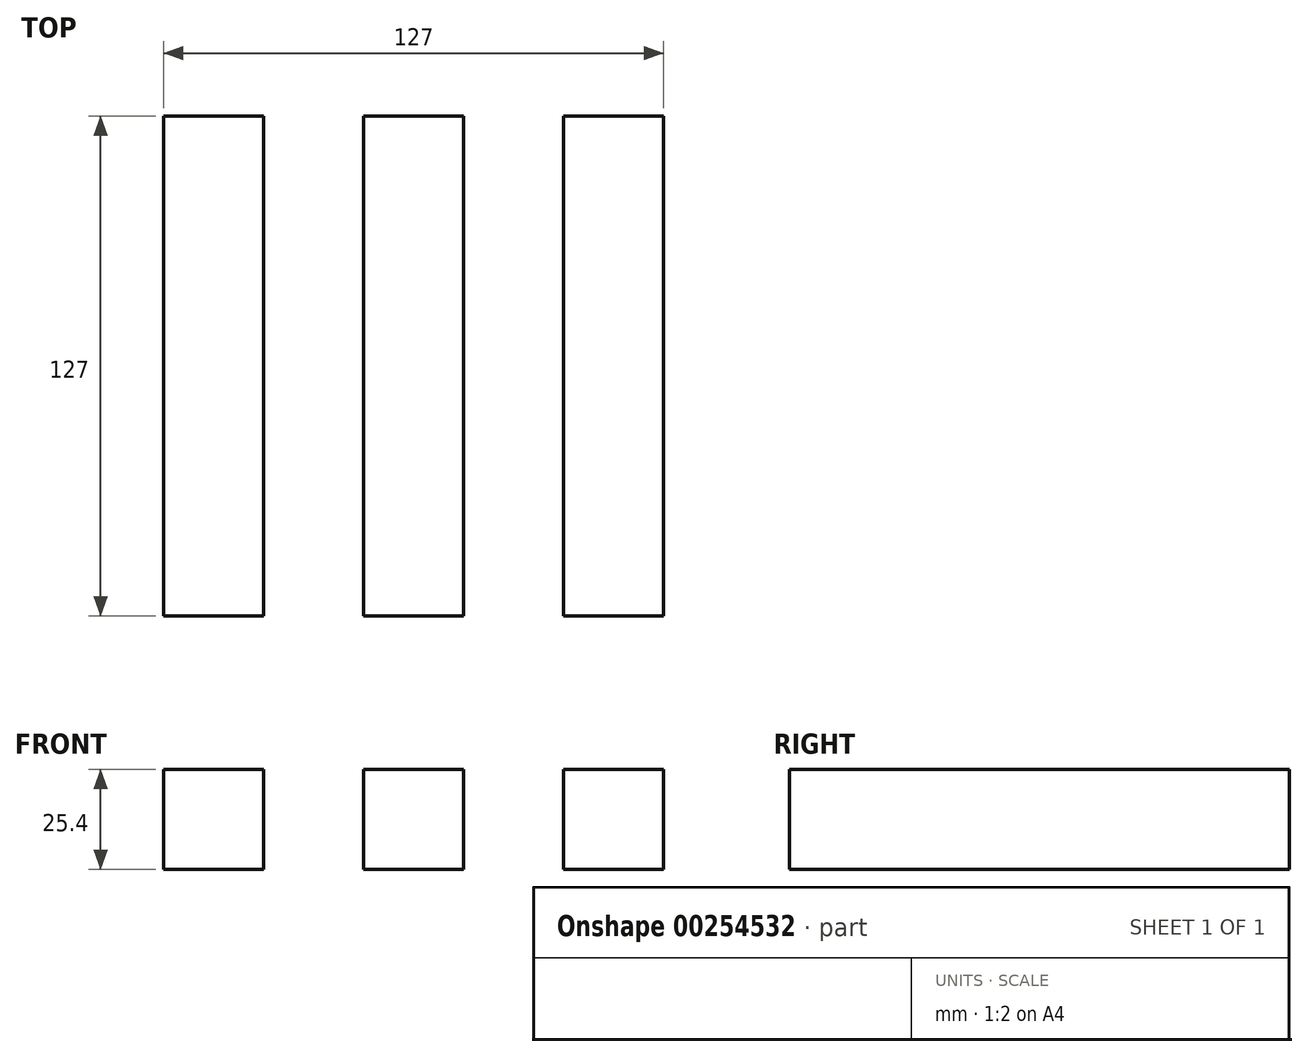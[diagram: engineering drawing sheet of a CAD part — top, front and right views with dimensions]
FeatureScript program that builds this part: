
annotation { "Feature Type Name" : "Feature", "Feature Type Description" : "" }
export const myFeature = defineFeature(function(context is Context, id is Id, definition is map)
    precondition{}
    {
        {
            var Q0;
            Q0=qCreatedBy(makeId("Front.planeOp"),FACE);
            var sketch = newSketch(context, id + "F0", { "sketchPlane" : qUnion([Q0])});
            skLineSegment(sketch, "E0.bottom", {"start": v(-12.7, 12.7) * mm, "end": v(12.7, 12.7) * mm});
            skLineSegment(sketch, "E0.top", {"start": v(-12.7, -12.7) * mm, "end": v(12.7, -12.7) * mm});
            skLineSegment(sketch, "E0.left", {"start": v(-12.7, 12.7) * mm, "end": v(-12.7, -12.7) * mm});
            skLineSegment(sketch, "E0.right", {"start": v(12.7, 12.7) * mm, "end": v(12.7, -12.7) * mm});
            skPoint(sketch, "E0.middle", {"position": v(0, 0) * mm});
            skLineSegment(sketch, "E1", {"start": v(0, 0) * mm, "end": v(-50.8, 0) * mm});
            skLineSegment(sketch, "E2", {"start": v(0, 0) * mm, "end": v(50.8, 0) * mm});
            skLineSegment(sketch, "E3.bottom", {"start": v(-38.1, -12.7) * mm, "end": v(-63.5, -12.7) * mm});
            skLineSegment(sketch, "E3.top", {"start": v(-38.1, 12.7) * mm, "end": v(-63.5, 12.7) * mm});
            skLineSegment(sketch, "E3.left", {"start": v(-38.1, -12.7) * mm, "end": v(-38.1, 12.7) * mm});
            skLineSegment(sketch, "E3.right", {"start": v(-63.5, -12.7) * mm, "end": v(-63.5, 12.7) * mm});
            skPoint(sketch, "E3.middle", {"position": v(-50.8, 0) * mm});
            skLineSegment(sketch, "E4.bottom", {"start": v(63.5, -12.7) * mm, "end": v(38.1, -12.7) * mm});
            skLineSegment(sketch, "E4.top", {"start": v(63.5, 12.7) * mm, "end": v(38.1, 12.7) * mm});
            skLineSegment(sketch, "E4.left", {"start": v(63.5, -12.7) * mm, "end": v(63.5, 12.7) * mm});
            skLineSegment(sketch, "E4.right", {"start": v(38.1, -12.7) * mm, "end": v(38.1, 12.7) * mm});
            skPoint(sketch, "E4.middle", {"position": v(50.8, 0) * mm});
            skSolve(sketch);
        }
        {
            var Q0;
            {var subQ1=sQuery(id+"F0.wireOp",EDGE,"E4.bottom");Q0=makeQuery(id+"F0.imprint","IMPRINT",FACE,{"disambiguationData":[TD([[makeQuery(id+"F0.imprint","IMPRINT",EDGE,{"derivedFrom":subQ1}),-1.0]])]});}
            var Q1;
            {var subQ6=sQuery(id+"F0.wireOp",EDGE,"E0.bottom");Q1=makeQuery(id+"F0.imprint","IMPRINT",FACE,{"disambiguationData":[TD([[makeQuery(id+"F0.imprint","IMPRINT",EDGE,{"derivedFrom":subQ6}),-1.0]])]});}
            var Q2;
            {var subQ6=sQuery(id+"F0.wireOp",EDGE,"E0.top");Q2=makeQuery(id+"F0.imprint","IMPRINT",FACE,{"disambiguationData":[TD([[makeQuery(id+"F0.imprint","IMPRINT",EDGE,{"derivedFrom":subQ6}),1.0]])]});}
            var Q3;
            {var subQ3=sQuery(id+"F0.wireOp",EDGE,"E3.bottom");Q3=makeQuery(id+"F0.imprint","IMPRINT",FACE,{"disambiguationData":[TD([[makeQuery(id+"F0.imprint","IMPRINT",EDGE,{"derivedFrom":subQ3}),-1.0]])]});}
            extrude(context, id + "F1", {"entities" : qUnion([Q0, Q1, Q2, Q3]), "endBound" : BoundingType.SYMMETRIC, "depth" : 127 * mm});
        }
    });
